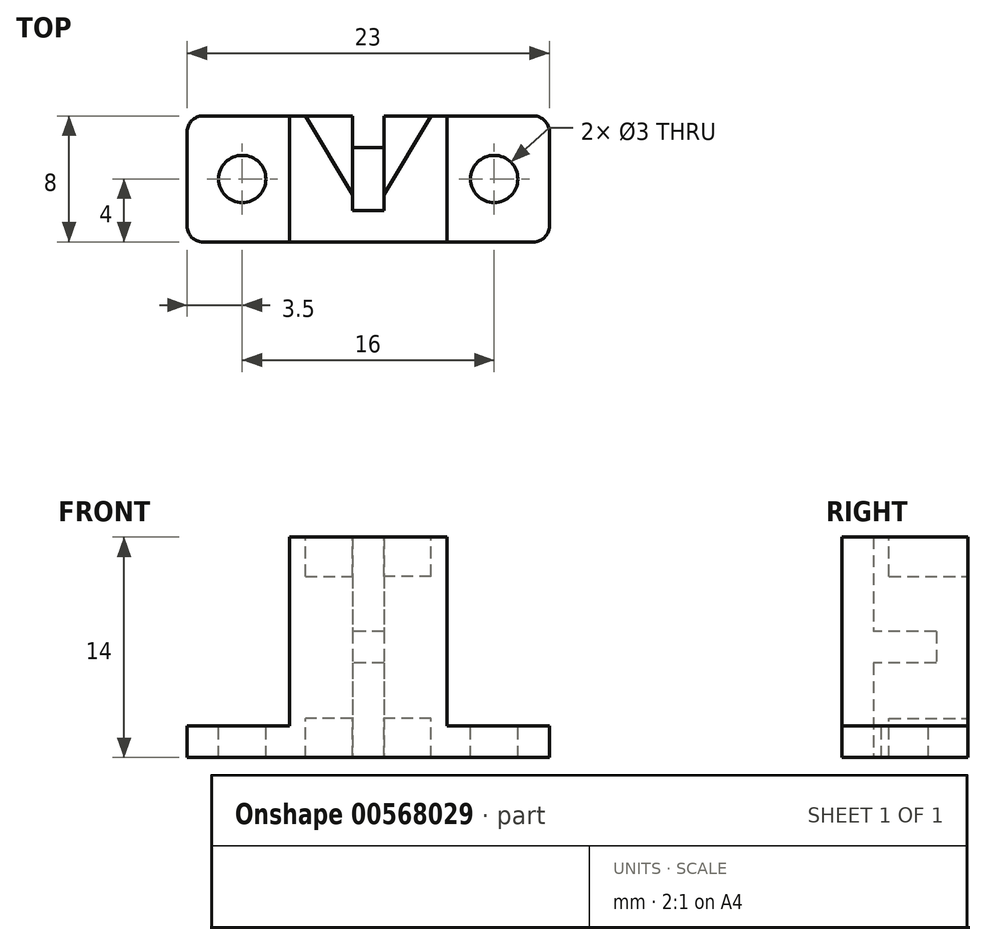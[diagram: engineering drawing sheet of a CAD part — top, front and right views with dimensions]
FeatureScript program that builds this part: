
annotation { "Feature Type Name" : "Feature", "Feature Type Description" : "" }
export const myFeature = defineFeature(function(context is Context, id is Id, definition is map)
    precondition{}
    {
        {
            var Q0;
            Q0=qCreatedBy(makeId("Top.planeOp"),FACE);
            var sketch = newSketch(context, id + "F0", { "sketchPlane" : qUnion([Q0])});
            skLineSegment(sketch, "E0", {"start": v(-11.5, 0) * mm, "end": v(11.5, 0) * mm});
            skLineSegment(sketch, "E1", {"start": v(11.5, 0) * mm, "end": v(11.5, 8) * mm});
            skLineSegment(sketch, "E2", {"start": v(11.5, 8) * mm, "end": v(1, 8) * mm});
            skLineSegment(sketch, "E3", {"start": v(1, 8) * mm, "end": v(1, 2) * mm});
            skLineSegment(sketch, "E4", {"start": v(1, 2) * mm, "end": v(-1, 2) * mm});
            skLineSegment(sketch, "E5", {"start": v(-1, 2) * mm, "end": v(-1, 8) * mm});
            skLineSegment(sketch, "E6", {"start": v(-1, 8) * mm, "end": v(-11.5, 8) * mm});
            skLineSegment(sketch, "E7", {"start": v(-11.5, 8) * mm, "end": v(-11.5, 0) * mm});
            skSolve(sketch);
        }
        {
            var Q0;
            Q0=makeQuery(id+"F0.imprint","IMPRINT",FACE,{"disambiguationData":[TD([[makeQuery(id+"F0.imprint","IMPRINT",EDGE,{"derivedFrom":sQuery(id+"F0.wireOp",EDGE,"E0")}),1.0]])]});
            extrude(context, id + "F1", {"entities" : qUnion([Q0]), "depth" : 2 * mm, "offsetDistance" : 25 * mm});
        }
        {
            var Q0;
            Q0=makeQuery(id+"F1.opExtrude","CAP_FACE",FACE,{"disambiguationData":[OSD([sQuery(id+"F0.wireOp",EDGE,"E0"),sQuery(id+"F0.wireOp",EDGE,"E1"),sQuery(id+"F0.wireOp",EDGE,"E2"),sQuery(id+"F0.wireOp",EDGE,"E3"),sQuery(id+"F0.wireOp",EDGE,"E4"),sQuery(id+"F0.wireOp",EDGE,"E5"),sQuery(id+"F0.wireOp",EDGE,"E6"),sQuery(id+"F0.wireOp",EDGE,"E7")])],"isStart":false});
            var sketch = newSketch(context, id + "F2", { "sketchPlane" : qUnion([Q0])});
            skLineSegment(sketch, "E8", {"start": v(-4, 8) * mm, "end": v(-1, 3) * mm});
            skLineSegment(sketch, "E9", {"start": v(4, 8) * mm, "end": v(1, 3) * mm});
            skSolve(sketch);
        }
        {
            var Q0;
            Q0 = qSketchRegion(id + "F2", true);
            var Q1;
            {var subQ0=sQuery(id+"F2.wireOp",EDGE,"E8");Q1=makeQuery(id+"F2.imprint","IMPRINT",FACE,{"disambiguationData":[TD([[makeQuery(id+"F2.imprint","IMPRINT",EDGE,{"derivedFrom":subQ0}),1.0]])]});}
            var Q2;
            {var subQ0=sQuery(id+"F2.wireOp",EDGE,"E9");Q2=makeQuery(id+"F2.imprint","IMPRINT",FACE,{"disambiguationData":[TD([[makeQuery(id+"F2.imprint","IMPRINT",EDGE,{"derivedFrom":subQ0}),-1.0]])]});}
            extrude(context, id + "F3", {"entities" : qUnion([Q0, Q1, Q2]), "operationType" : NewBodyOperationType.REMOVE, "oppositeDirection" : true, "depth" : 25 * mm, "offsetDistance" : 25 * mm});
        }
        {
            var Q0;
            Q0=makeQuery(id+"F1.opExtrude","CAP_FACE",FACE,{"disambiguationData":[OSD([sQuery(id+"F0.wireOp",EDGE,"E0"),sQuery(id+"F0.wireOp",EDGE,"E1"),sQuery(id+"F0.wireOp",EDGE,"E2"),sQuery(id+"F0.wireOp",EDGE,"E3"),sQuery(id+"F0.wireOp",EDGE,"E4"),sQuery(id+"F0.wireOp",EDGE,"E5"),sQuery(id+"F0.wireOp",EDGE,"E6"),sQuery(id+"F0.wireOp",EDGE,"E7")])],"isStart":false});
            var sketch = newSketch(context, id + "F4", { "sketchPlane" : qUnion([Q0])});
            skCircle(sketch, "E10", {"center": v(8, 4) * mm, "radius": 1.5 * mm});
            skCircle(sketch, "E11", {"center": v(-8, 4) * mm, "radius": 1.5 * mm});
            skSolve(sketch);
        }
        {
            var Q0;
            Q0=makeQuery(id+"F4.imprint","IMPRINT",FACE,{"disambiguationData":[TD([[makeQuery(id+"F4.imprint","IMPRINT",EDGE,{"derivedFrom":sQuery(id+"F4.wireOp",EDGE,"E11")}),1.0]])]});
            var Q1;
            Q1=makeQuery(id+"F4.imprint","IMPRINT",FACE,{"disambiguationData":[TD([[makeQuery(id+"F4.imprint","IMPRINT",EDGE,{"derivedFrom":sQuery(id+"F4.wireOp",EDGE,"E10")}),1.0]])]});
            extrude(context, id + "F5", {"entities" : qUnion([Q0, Q1]), "operationType" : NewBodyOperationType.REMOVE, "oppositeDirection" : true, "depth" : 25 * mm, "offsetDistance" : 25 * mm});
        }
        {
            var Q0;
            Q0=makeQuery(id+"F1.opExtrude","CAP_FACE",FACE,{"disambiguationData":[OSD([sQuery(id+"F0.wireOp",EDGE,"E0"),sQuery(id+"F0.wireOp",EDGE,"E1"),sQuery(id+"F0.wireOp",EDGE,"E2"),sQuery(id+"F0.wireOp",EDGE,"E3"),sQuery(id+"F0.wireOp",EDGE,"E4"),sQuery(id+"F0.wireOp",EDGE,"E5"),sQuery(id+"F0.wireOp",EDGE,"E6"),sQuery(id+"F0.wireOp",EDGE,"E7")])],"isStart":false});
            var sketch = newSketch(context, id + "F6", { "sketchPlane" : qUnion([Q0])});
            skLineSegment(sketch, "E12", {"start": v(-5, 8) * mm, "end": v(-5, 0) * mm});
            skLineSegment(sketch, "E13", {"start": v(-5, 0) * mm, "end": v(5, 0) * mm});
            skLineSegment(sketch, "E14", {"start": v(5, 0) * mm, "end": v(5, 8) * mm});
            skSolve(sketch);
        }
        {
            var Q0;
            {var subQ3=sQuery(id+"F6.wireOp",EDGE,"E12");Q0=makeQuery(id+"F6.imprint","IMPRINT",FACE,{"disambiguationData":[TD([[makeQuery(id+"F6.imprint","IMPRINT",EDGE,{"derivedFrom":subQ3}),1.0]])]});}
            extrude(context, id + "F7", {"entities" : qUnion([Q0]), "operationType" : NewBodyOperationType.ADD, "depth" : 12 * mm, "offsetDistance" : 25 * mm});
        }
        {
            var Q0;
            {var subQ0=sQuery(id+"F0.wireOp",EDGE,"E6");Q0=makeQuery(id+"F7.boolean.opBoolean","MERGE",FACE,{"derivedFrom":[makeQuery(id+"F1.opExtrude","SWEPT_FACE",FACE,{"disambiguationData":[OSD([subQ0])]}),makeQuery(id+"F7.opExtrude","SWEPT_FACE",FACE,{"disambiguationData":[OSD([subQ0])]})]});}
            var sketch = newSketch(context, id + "F8", { "sketchPlane" : qUnion([Q0])});
            skLineSegment(sketch, "E15.bottom", {"start": v(4, 11.5) * mm, "end": v(1, 11.5) * mm});
            skLineSegment(sketch, "E15.top", {"start": v(4, 2.5) * mm, "end": v(1, 2.5) * mm});
            skLineSegment(sketch, "E15.left", {"start": v(4, 11.5) * mm, "end": v(4, 2.5) * mm});
            skLineSegment(sketch, "E15.right", {"start": v(1, 11.5) * mm, "end": v(1, 2.5) * mm});
            skLineSegment(sketch, "E16.0", {"start": v(-4, 0) * mm, "end": v(-4, 14) * mm});
            skLineSegment(sketch, "E17.bottom", {"start": v(-4, 11.5) * mm, "end": v(-1, 11.5) * mm});
            skLineSegment(sketch, "E17.top", {"start": v(-4, 2.5) * mm, "end": v(-1, 2.5) * mm});
            skLineSegment(sketch, "E17.left", {"start": v(-4, 11.5) * mm, "end": v(-4, 2.5) * mm});
            skLineSegment(sketch, "E17.right", {"start": v(-1, 11.5) * mm, "end": v(-1, 2.5) * mm});
            skSolve(sketch);
        }
        {
            var Q0;
            Q0 = qSketchRegion(id + "F8", true);
            extrude(context, id + "F9", {"entities" : qUnion([Q0]), "operationType" : NewBodyOperationType.ADD, "oppositeDirection" : true, "depth" : 8 * mm, "offsetDistance" : 25 * mm});
        }
        {
            var Q0;
            {var subQ0=sQuery(id+"F0.wireOp",EDGE,"E4");Q0=makeQuery(id+"F7.boolean.opBoolean","MERGE",FACE,{"derivedFrom":[makeQuery(id+"F1.opExtrude","SWEPT_FACE",FACE,{"disambiguationData":[OSD([subQ0])]}),makeQuery(id+"F7.opExtrude","SWEPT_FACE",FACE,{"disambiguationData":[OSD([subQ0])]})]});}
            var sketch = newSketch(context, id + "F10", { "sketchPlane" : qUnion([Q0])});
            skLineSegment(sketch, "E18.bottom", {"start": v(-1, 6) * mm, "end": v(1, 6) * mm});
            skLineSegment(sketch, "E18.top", {"start": v(-1, 8) * mm, "end": v(1, 8) * mm});
            skLineSegment(sketch, "E18.left", {"start": v(-1, 6) * mm, "end": v(-1, 8) * mm});
            skLineSegment(sketch, "E18.right", {"start": v(1, 6) * mm, "end": v(1, 8) * mm});
            skSolve(sketch);
        }
        {
            var Q0;
            Q0 = qSketchRegion(id + "F10", true);
            extrude(context, id + "F11", {"entities" : qUnion([Q0]), "operationType" : NewBodyOperationType.ADD, "depth" : 4 * mm, "offsetDistance" : 25 * mm});
        }
        {
            var Q0;
            Q0=makeQuery(id+"F1.opExtrude","SWEPT_EDGE",EDGE,{"disambiguationData":[OSD([sQuery(id+"F0.wireOp",EDGE,"E1"),sQuery(id+"F0.wireOp",EDGE,"E2")])]});
            var Q1;
            Q1=makeQuery(id+"F1.opExtrude","SWEPT_EDGE",EDGE,{"disambiguationData":[OSD([sQuery(id+"F0.wireOp",EDGE,"E0"),sQuery(id+"F0.wireOp",EDGE,"E1")])]});
            var Q2;
            Q2=makeQuery(id+"F1.opExtrude","SWEPT_EDGE",EDGE,{"disambiguationData":[OSD([sQuery(id+"F0.wireOp",EDGE,"E0"),sQuery(id+"F0.wireOp",EDGE,"E7")])]});
            var Q3;
            Q3=makeQuery(id+"F1.opExtrude","SWEPT_EDGE",EDGE,{"disambiguationData":[OSD([sQuery(id+"F0.wireOp",EDGE,"E6"),sQuery(id+"F0.wireOp",EDGE,"E7")])]});
            fillet(context, id + "F12", {"entities" : qUnion([Q0, Q1, Q2, Q3]), "radius" : 1 * mm, "tangentPropagation" : true, "allowEdgeOverflow" : false});
        }
    });
